# Revit family: Sensor-Lutron-Wall-Radio_Powr_Savr-Vacancy-LRF2-VHLB-P-WH
name_source: partatom
category: Lighting Devices
units: mm (PartAtom-declared; Revit-internal decimal feet)

## family parameters
Cut with Voids When Loaded = No
Host = Face
Maintain Annotation Orientation = No
OmniClass Number = 23.85.80.11.27
OmniClass Title = Lighting Controls
Part Type = Normal
Room Calculation Point = No
Round Connector Dimension = Use Diameter
Shared = No

## types (1)
- LRF2-VHLB-P-WH
    Assembly Code = D5030800
    Coverage = 0 SF
    Coverage Area = Major motion = coverage of up to 150 ft (45.7 m)
    Default Elevation = 48 "
    Depth = 1.35 "
    Description = Wall-mounted occupancy and vacancy sensor
    Field of View = 0.00°
    Finish = Plastic - Lutron - White
    Instruction Sheet Link = https://assets.lutron.com
    Keynote = 16500
    Length = 4.35 "
    Manufacturer = Lutron Electronics Co., Inc
    Manufacturer Fax Number = 610-282-1243
    Maximum Operating Temperature = 104 °F / 40 °C
    Minimum Operating Temperature = 32 °F / 0 °C
    Model = LRF2-VHLB-P-WH
    Number of Poles = 1
    Performance URL = https://www.lutron.com
    Power Factor = 1
    Product Documentation Link = https://assets.lutron.com
    Product Name = Radio Powr Savr Wireless Vacancy Wall-Mount Sensor
    Product Page URL = https://www.lutron.com
    Sensor Type = Vacancy
    Series = Radio Powr Savr
    URL = http://www.lutron.com
    Version = 2021 - v1.0a
    Video Link = https://www.youtube.com
    Voltage = 3 V
    Voltage Comment = Operating Voltage: 3 V
    Warranty URL = https://www.lutron.com
    Width = 1.8 "

## geometry (parser evidence)
native form markers: Sweep x4
no freeform markers — native parametric forms only
